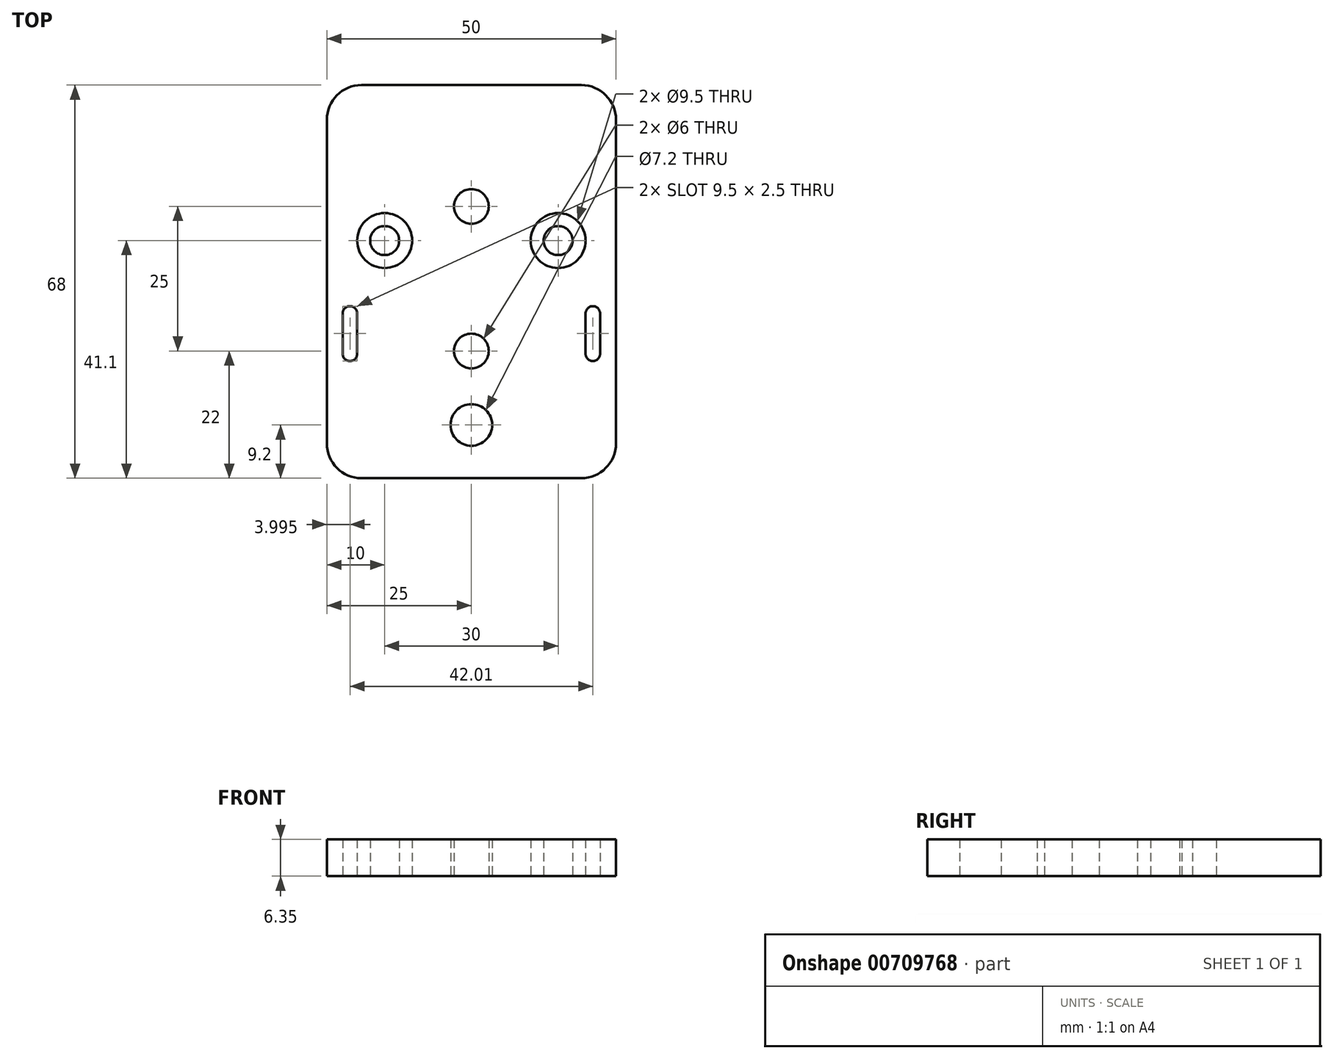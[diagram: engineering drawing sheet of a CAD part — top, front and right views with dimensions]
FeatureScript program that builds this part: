
annotation { "Feature Type Name" : "Feature", "Feature Type Description" : "" }
export const myFeature = defineFeature(function(context is Context, id is Id, definition is map)
    precondition{}
    {
        {
            var Q0;
            Q0=qCreatedBy(makeId("Top.planeOp"),FACE);
            var sketch = newSketch(context, id + "F0", { "sketchPlane" : qUnion([Q0])});
            skLineSegment(sketch, "E0", {"start": v(-22.26, -5.5) * mm, "end": v(-25, -5.5) * mm});
            skLineSegment(sketch, "E1", {"start": v(19.75, -5.5) * mm, "end": v(19.75, -12.5) * mm});
            skLineSegment(sketch, "E2", {"start": v(22.25, -12.5) * mm, "end": v(22.25, -5.5) * mm});
            skLineSegment(sketch, "E3", {"start": v(-22.26, -5.5) * mm, "end": v(-22.26, -12.5) * mm});
            skLineSegment(sketch, "E4", {"start": v(-19.76, -12.5) * mm, "end": v(-19.76, -5.5) * mm});
            skArc(sketch, "E5", {"start": v(19, -34) * mm, "mid": v(23.24, -32.24) * mm, "end": v(25, -28) * mm});
            skArc(sketch, "E6", {"start": v(-25, -28) * mm, "mid": v(-23.24, -32.24) * mm, "end": v(-19, -34) * mm});
            skLineSegment(sketch, "E7", {"start": v(-19, -34) * mm, "end": v(-10, -34) * mm});
            skLineSegment(sketch, "E8", {"start": v(19, -34) * mm, "end": v(-10, -34) * mm});
            skCircle(sketch, "E9", {"center": v(-15, 7.1) * mm, "radius": 2.5 * mm});
            skCircle(sketch, "E10", {"center": v(15, 7.1) * mm, "radius": 2.5 * mm});
            skLineSegment(sketch, "E11", {"start": v(-25, 28) * mm, "end": v(-25, -28) * mm});
            skArc(sketch, "E12", {"start": v(-19, 34) * mm, "mid": v(-23.24, 32.24) * mm, "end": v(-25, 28) * mm});
            skLineSegment(sketch, "E13", {"start": v(19, 34) * mm, "end": v(-19, 34) * mm});
            skLineSegment(sketch, "E14", {"start": v(25, 28) * mm, "end": v(25, -28) * mm});
            skArc(sketch, "E15", {"start": v(25, 28) * mm, "mid": v(23.24, 32.24) * mm, "end": v(19, 34) * mm});
            skCircle(sketch, "E16", {"center": v(0, -24.8) * mm, "radius": 6 * mm});
            skCircle(sketch, "E17", {"center": v(-15, 7.1) * mm, "radius": 4.75 * mm});
            skCircle(sketch, "E18", {"center": v(15, 7.1) * mm, "radius": 4.75 * mm});
            skLineSegment(sketch, "E19", {"start": v(-9.6, 34) * mm, "end": v(-9.6, -34) * mm});
            skLineSegment(sketch, "E20", {"start": v(9.6, 34) * mm, "end": v(9.6, -34) * mm});
            skLineSegment(sketch, "E21", {"start": v(-22.26, -12.5) * mm, "end": v(-25, -12.5) * mm});
            skLineSegment(sketch, "E22", {"start": v(22.25, -12.5) * mm, "end": v(25, -12.5) * mm});
            skLineSegment(sketch, "E23", {"start": v(22.25, -5.5) * mm, "end": v(25, -5.5) * mm});
            skCircle(sketch, "E24", {"center": v(0, -12) * mm, "radius": 3 * mm});
            skCircle(sketch, "E25", {"center": v(0, -12) * mm, "radius": 2.5 * mm});
            skCircle(sketch, "E26", {"center": v(0, 13) * mm, "radius": 2.5 * mm});
            skCircle(sketch, "E27", {"center": v(0, 13) * mm, "radius": 3 * mm});
            skCircle(sketch, "E28", {"center": v(0, -24.8) * mm, "radius": 3.6 * mm});
            skArc(sketch, "E29", {"start": v(-19.76, -5.5) * mm, "mid": v(-21, -4.25) * mm, "end": v(-22.26, -5.5) * mm});
            skArc(sketch, "E30", {"start": v(-22.26, -12.5) * mm, "mid": v(-21, -13.75) * mm, "end": v(-19.76, -12.5) * mm});
            skArc(sketch, "E31", {"start": v(22.25, -5.5) * mm, "mid": v(21, -4.25) * mm, "end": v(19.75, -5.5) * mm});
            skArc(sketch, "E32", {"start": v(19.75, -12.5) * mm, "mid": v(21, -13.75) * mm, "end": v(22.25, -12.5) * mm});
            skSolve(sketch);
        }
        {
            var Q0;
            Q0=makeQuery(id+"F0.imprint","IMPRINT",FACE,{"disambiguationData":[TD([[makeQuery(id+"F0.imprint","IMPRINT",EDGE,{"derivedFrom":sQuery(id+"F0.wireOp",EDGE,"E16")}),1.0]])]});
            var Q1;
            {var subQ4=sQuery(id+"F0.wireOp",EDGE,"E0");Q1=makeQuery(id+"F0.imprint","IMPRINT",FACE,{"disambiguationData":[TD([[makeQuery(id+"F0.imprint","IMPRINT",EDGE,{"derivedFrom":subQ4}),-1.0]])]});}
            var Q2;
            Q2=makeQuery(id+"F0.imprint","IMPRINT",FACE,{"disambiguationData":[TD([[makeQuery(id+"F0.imprint","IMPRINT",EDGE,{"derivedFrom":sQuery(id+"F0.wireOp",EDGE,"E1")}),-1.0]])]});
            var Q3;
            Q3=makeQuery(id+"F0.imprint","IMPRINT",FACE,{"disambiguationData":[TD([[makeQuery(id+"F0.imprint","IMPRINT",EDGE,{"derivedFrom":sQuery(id+"F0.wireOp",EDGE,"E16")}),-1.0]])]});
            var Q4;
            Q4=makeQuery(id+"F0.imprint","IMPRINT",FACE,{"disambiguationData":[TD([[makeQuery(id+"F0.imprint","IMPRINT",EDGE,{"derivedFrom":sQuery(id+"F0.wireOp",EDGE,"E10")}),1.0]])]});
            var Q5;
            Q5=makeQuery(id+"F0.imprint","IMPRINT",FACE,{"disambiguationData":[TD([[makeQuery(id+"F0.imprint","IMPRINT",EDGE,{"derivedFrom":sQuery(id+"F0.wireOp",EDGE,"E9")}),1.0]])]});
            var Q6;
            {var subQ0=sQuery(id+"F0.wireOp",EDGE,"E0");Q6=makeQuery(id+"F0.imprint","IMPRINT",FACE,{"disambiguationData":[TD([[makeQuery(id+"F0.imprint","IMPRINT",EDGE,{"derivedFrom":subQ0}),1.0]])]});}
            var Q7;
            Q7=makeQuery(id+"F0.imprint","IMPRINT",FACE,{"disambiguationData":[TD([[makeQuery(id+"F0.imprint","IMPRINT",EDGE,{"derivedFrom":sQuery(id+"F0.wireOp",EDGE,"E2")}),-1.0]])]});
            extrude(context, id + "F1", {"entities" : qUnion([Q0, Q1, Q2, Q3, Q4, Q5, Q6, Q7]), "depth" : 6.35 * mm, "offsetDistance" : 25 * mm});
        }
    });
